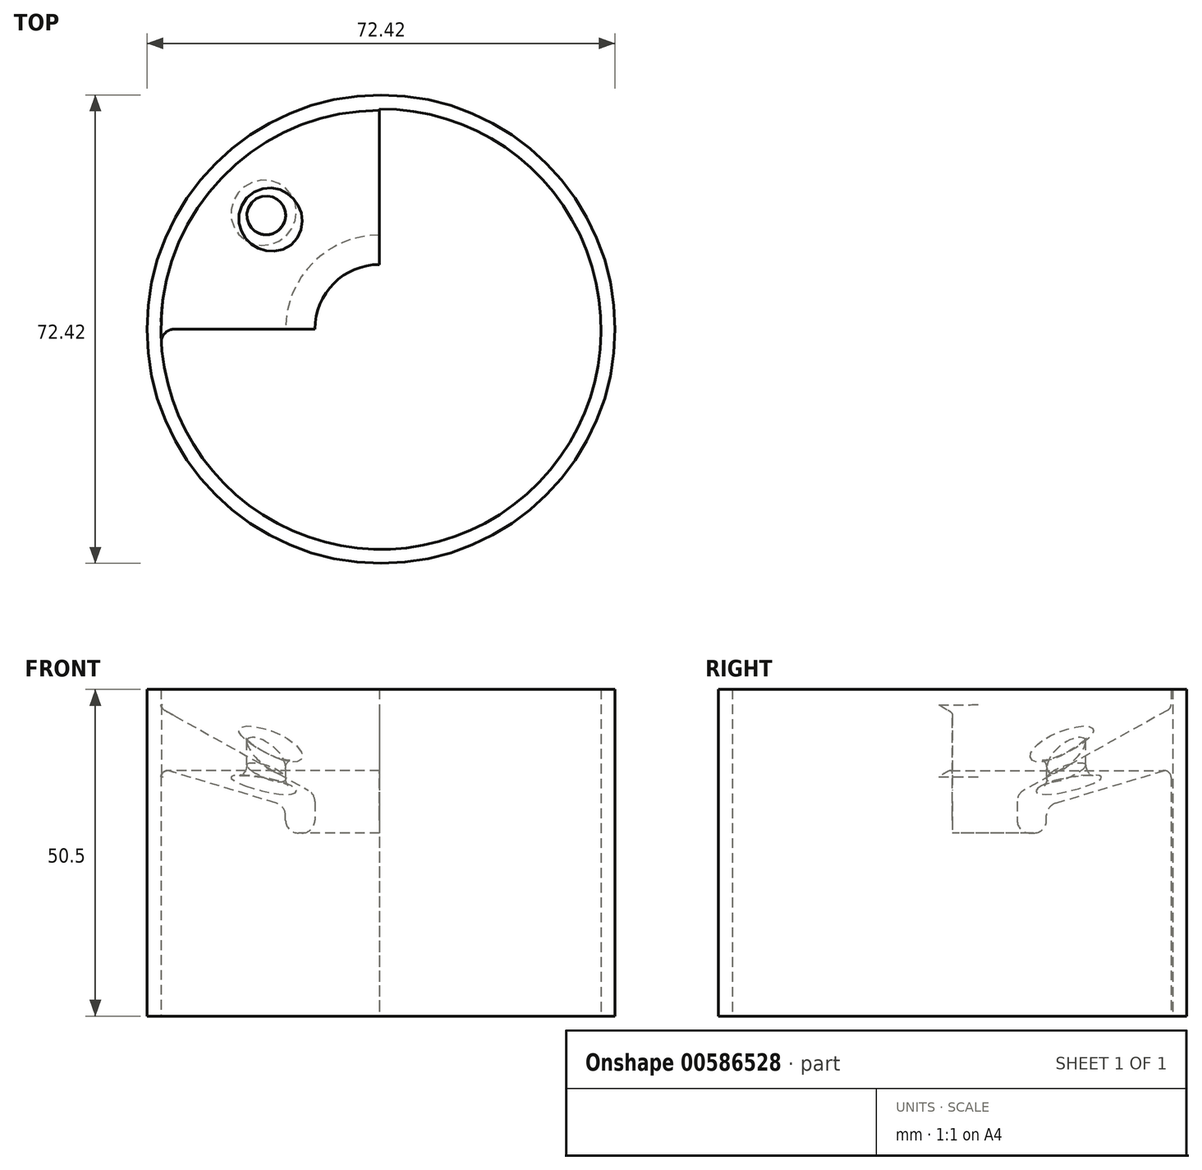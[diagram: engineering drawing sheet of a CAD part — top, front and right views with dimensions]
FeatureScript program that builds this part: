
annotation { "Feature Type Name" : "Feature", "Feature Type Description" : "" }
export const myFeature = defineFeature(function(context is Context, id is Id, definition is map)
    precondition{}
    {
        {
            var Q0;
            Q0=qCreatedBy(makeId("Front.planeOp"),FACE);
            var sketch = newSketch(context, id + "F0", { "sketchPlane" : qUnion([Q0])});
            skLineSegment(sketch, "E0.bottom", {"start": v(-36.16, 50.5) * mm, "end": v(-34.05, 50.5) * mm});
            skLineSegment(sketch, "E0.top", {"start": v(-36.16, 0) * mm, "end": v(-34.05, 0) * mm});
            skLineSegment(sketch, "E0.left", {"start": v(-36.16, 50.5) * mm, "end": v(-36.16, 0) * mm});
            skLineSegment(sketch, "E0.right", {"start": v(-34.05, 36.95) * mm, "end": v(-34.05, 0) * mm});
            skLineSegment(sketch, "E1", {"start": v(-33.54, 47.31) * mm, "end": v(-11.26, 34.91) * mm});
            skLineSegment(sketch, "E2", {"start": v(-10.23, 33.17) * mm, "end": v(-10.23, 30.3) * mm});
            skLineSegment(sketch, "E3", {"start": v(-12.23, 28.3) * mm, "end": v(-12.77, 28.3) * mm});
            skLineSegment(sketch, "E4", {"start": v(-14.77, 30.3) * mm, "end": v(-14.77, 31) * mm});
            skLineSegment(sketch, "E5", {"start": v(-16.2, 32.92) * mm, "end": v(-32.76, 37.9) * mm});
            skPoint(sketch, "E6.visualSharp", {"position": v(-14.77, 32.5) * mm});
            skArc(sketch, "E6.filletArc", {"start": v(-14.77, 31) * mm, "mid": v(-15.16, 32.2) * mm, "end": v(-16.2, 32.92) * mm});
            skPoint(sketch, "E7.visualSharp", {"position": v(-14.77, 28.3) * mm});
            skArc(sketch, "E7.filletArc", {"start": v(-14.77, 30.3) * mm, "mid": v(-14.18, 28.88) * mm, "end": v(-12.77, 28.3) * mm});
            skPoint(sketch, "E8.visualSharp", {"position": v(-10.23, 28.3) * mm});
            skArc(sketch, "E8.filletArc", {"start": v(-12.23, 28.3) * mm, "mid": v(-10.82, 28.88) * mm, "end": v(-10.23, 30.3) * mm});
            skPoint(sketch, "E9.visualSharp", {"position": v(-10.23, 34.34) * mm});
            skArc(sketch, "E9.filletArc", {"start": v(-10.23, 33.17) * mm, "mid": v(-10.5, 34.18) * mm, "end": v(-11.26, 34.91) * mm});
            skArc(sketch, "E10.filletArc", {"start": v(-32.76, 37.9) * mm, "mid": v(-33.65, 37.75) * mm, "end": v(-34.05, 36.95) * mm});
            skLineSegment(sketch, "E11", {"start": v(-34.05, 50.5) * mm, "end": v(-34.05, 48.19) * mm});
            skPoint(sketch, "E12.visualSharp", {"position": v(-34.05, 47.6) * mm});
            skArc(sketch, "E12.filletArc", {"start": v(-34.05, 48.19) * mm, "mid": v(-33.91, 47.68) * mm, "end": v(-33.54, 47.31) * mm});
            skLineSegment(sketch, "E13", {"start": v(-0.23, 50.5) * mm, "end": v(-0.23, 0) * mm, "construction": true});
            skSolve(sketch);
        }
        {
            var Q0;
            Q0=makeQuery(id+"F0.imprint","IMPRINT",FACE,{"disambiguationData":[TD([[makeQuery(id+"F0.imprint","IMPRINT",EDGE,{"derivedFrom":sQuery(id+"F0.wireOp",EDGE,"E0.bottom")}),-1.0]])]});
            var Q1;
            Q1=sQuery(id+"F0.wireOp",EDGE,"E13");
            revolve(context, id + "F1", {"entities" : qUnion([Q0]), "axis" : qUnion([Q1]), "revolveType" : RevolveType.ONE_DIRECTION, "angle" : 90 * degree});
        }
        {
            var Q0;
            Q0=makeQuery(id+"F1.opRevolve","SWEPT_FACE",FACE,{"disambiguationData":[OSD([sQuery(id+"F0.wireOp",EDGE,"E0.bottom")])]});
            var sketch = newSketch(context, id + "F2", { "sketchPlane" : qUnion([Q0])});
            skLineSegment(sketch, "E14", {"start": v(0, 0) * mm, "end": v(-25.63, 25.4) * mm, "construction": true});
            skCircle(sketch, "E15", {"center": v(-17.76, 17.6) * mm, "radius": 3 * mm});
            skSolve(sketch);
        }
        {
            var Q0;
            Q0=makeQuery(id+"F2.imprint","IMPRINT",FACE,{"disambiguationData":[TD([[makeQuery(id+"F2.imprint","IMPRINT",EDGE,{"derivedFrom":sQuery(id+"F2.wireOp",EDGE,"E15")}),1.0]])]});
            extrude(context, id + "F3", {"entities" : qUnion([Q0]), "operationType" : NewBodyOperationType.REMOVE, "oppositeDirection" : true, "depth" : 46.8 * mm, "offsetDistance" : 25 * mm});
        }
        {
            var Q0;
            Q0=makeQuery(id+"F3.boolean.opBoolean","INTERSECT",EDGE,{"derivedFrom":[makeQuery(id+"F1.opRevolve","SWEPT_FACE",FACE,{"disambiguationData":[OSD([sQuery(id+"F0.wireOp",EDGE,"E1")])]}),makeQuery(id+"F3.opExtrude","SWEPT_FACE",FACE,{"disambiguationData":[OSD([sQuery(id+"F2.wireOp",EDGE,"E15")])]})]});
            fillet(context, id + "F4", {"entities" : qUnion([Q0]), "radius" : 2 * mm, "tangentPropagation" : true, "allowEdgeOverflow" : false});
        }
        {
            var Q0;
            Q0=makeQuery(id+"F3.boolean.opBoolean","INTERSECT",EDGE,{"derivedFrom":[makeQuery(id+"F1.opRevolve","SWEPT_FACE",FACE,{"disambiguationData":[OSD([sQuery(id+"F0.wireOp",EDGE,"E5")])]}),makeQuery(id+"F3.opExtrude","SWEPT_FACE",FACE,{"disambiguationData":[OSD([sQuery(id+"F2.wireOp",EDGE,"E15")])]})]});
            fillet(context, id + "F5", {"entities" : qUnion([Q0]), "radius" : 2 * mm, "tangentPropagation" : true, "allowEdgeOverflow" : false});
        }
        {
            var Q0;
            Q0=qCreatedBy(makeId("Top.planeOp"),FACE);
            var sketch = newSketch(context, id + "F6", { "sketchPlane" : qUnion([Q0])});
            skCircle(sketch, "E16", {"center": v(0, 0) * mm, "radius": 36.2 * mm});
            skCircle(sketch, "E17", {"center": v(0, 0) * mm, "radius": 34.05 * mm});
            skSolve(sketch);
        }
        {
            var Q0;
            Q0=makeQuery(id+"F6.imprint","IMPRINT",FACE,{"disambiguationData":[TD([[makeQuery(id+"F6.imprint","IMPRINT",EDGE,{"derivedFrom":sQuery(id+"F6.wireOp",EDGE,"E16")}),1.0]])]});
            var Q1;
            Q1=makeQuery(id+"F1.opRevolve","SWEPT_FACE",FACE,{"disambiguationData":[OSD([sQuery(id+"F0.wireOp",EDGE,"E0.bottom")])]});
            extrude(context, id + "F7", {"entities" : qUnion([Q0]), "operationType" : NewBodyOperationType.ADD, "endBound" : BoundingType.UP_TO_SURFACE, "depth" : 36.2 * mm, "endBoundEntityFace" : qUnion([Q1]), "offsetDistance" : 25 * mm});
        }
        {
            var Q0;
            Q0=makeQuery(id+"F7.boolean.opBoolean","INTERSECT",EDGE,{"derivedFrom":[makeQuery(id+"F1.opRevolve","CAP_FACE",FACE,{"disambiguationData":[OSD([sQuery(id+"F0.wireOp",EDGE,"E0.bottom"),sQuery(id+"F0.wireOp",EDGE,"E0.top"),sQuery(id+"F0.wireOp",EDGE,"E0.left"),sQuery(id+"F0.wireOp",EDGE,"E0.right"),sQuery(id+"F0.wireOp",EDGE,"E1"),sQuery(id+"F0.wireOp",EDGE,"E2"),sQuery(id+"F0.wireOp",EDGE,"E3"),sQuery(id+"F0.wireOp",EDGE,"E4"),sQuery(id+"F0.wireOp",EDGE,"E5"),sQuery(id+"F0.wireOp",EDGE,"E6.filletArc"),sQuery(id+"F0.wireOp",EDGE,"E7.filletArc"),sQuery(id+"F0.wireOp",EDGE,"E8.filletArc"),sQuery(id+"F0.wireOp",EDGE,"E9.filletArc"),sQuery(id+"F0.wireOp",EDGE,"E10.filletArc"),sQuery(id+"F0.wireOp",EDGE,"E11"),sQuery(id+"F0.wireOp",EDGE,"E12.filletArc")])],"isStart":true}),makeQuery(id+"F7.opExtrude","SWEPT_FACE",FACE,{"disambiguationData":[OSD([sQuery(id+"F6.wireOp",EDGE,"E17")])]})]});
            fillet(context, id + "F8", {"entities" : qUnion([Q0]), "radius" : 2 * mm, "tangentPropagation" : true, "allowEdgeOverflow" : false});
        }
    });
